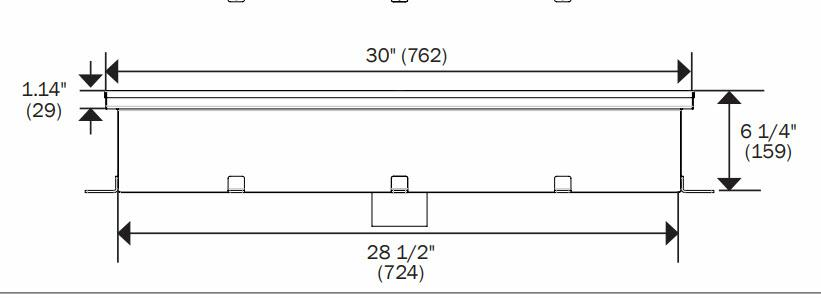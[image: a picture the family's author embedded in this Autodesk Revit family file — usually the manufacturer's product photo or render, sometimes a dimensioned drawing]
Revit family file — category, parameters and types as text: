
# Revit family: P5000
name_source: partatom
category: Plumbing Fixtures
revit_build: Autodesk Revit 2018 (Build: 20170223_1515(x64)
units: mm (PartAtom-declared; Revit-internal decimal feet)

## family parameters
Cut with Voids When Loaded = No
Host = Face
Part Type = Normal
Room Calculation Point = No
Round Connector Dimension = Use Radius
Shared = No

## types (36) — shared parameters
Banding = Yes
Banding Thickness = 0' - 0 1/8"
Cross Bar Offset = 0' - 2"
Cross Bar Spacing = 0' - 2"
Cross Bar Thickness = 0' - 0 1/8"
Default Elevation = 0' - 0"
Description = STAINLESS STEEL KETTLE DRAIN
Grate and Frame
Floor Drain Material = Paint - Sherwin Williams Paint - #952C2A - Bellwood Red
Height of Grating = 0' - 1 3/8"
Manufacturer = MIFAB
Material = Metal - Steel - ASTM A36
Support Bar Offset = 0' - 0 1/8"
Support Bar Spacing = 0' - 1"
Support Bar Thickness = 0' - 0 1/8"
URL = WWW.MIFAB.COM
zero-valued in all types: CWFU, WFU

## per-type parameters (varying)
| type | Length | Length2 | Model | Number of Cross Bars | Number of Support Bars | Pipe Radius | Support Bar Length | Width | Width2 |
| P5001 - 12" x 24" | 2' - 0" | 1' - 11 3/4" | P5001 | 5 | 24 | 0' - 2" | 0' - 11 1/2" | 1' - 0" | 0' - 11 3/4" |
| P5002 - 12" x 30" | 2' - 6" | 2' - 5 3/4" | P5002 | 5 | 30 | 0' - 2" | 0' - 11 1/2" | 1' - 0" | 0' - 11 3/4" |
| P5003 - 12" x 36" | 3' - 0" | 2' - 11 3/4" | P5003 | 5 | 36 | 0' - 2" | 0' - 11 1/2" | 1' - 0" | 0' - 11 3/4" |
| P5004 - 12" x 48" | 4' - 0" | 3' - 11 3/4" | P5004 | 5 | 48 | 0' - 2" | 0' - 11 1/2" | 1' - 0" | 0' - 11 3/4" |
| P5004 -60 - 12" x 60" | 5' - 0" | 4' - 11 3/4" | P5004-60 | 5 | 60 | 0' - 2" | 0' - 11 1/2" | 1' - 0" | 0' - 11 3/4" |
| P5004-72 - 12" x 72" | 6' - 0" | 5' - 11 3/4" | P5004-72 | 5 | 72 | 0' - 2" | 0' - 11 1/2" | 1' - 0" | 0' - 11 3/4" |
| P5004-84- 12" x 84" | 7' - 0" | 6' - 11 3/4" | P5004-84 | 5 | 84 | 0' - 2" | 0' - 11 1/2" | 1' - 0" | 0' - 11 3/4" |
| P5004-96 - 12" x 96" | 8' - 0" | 7' - 11 3/4" | P5004-96 | 5 | 96 | 0' - 2" | 0' - 11 1/2" | 1' - 0" | 0' - 11 3/4" |
| P5004-108 - 12" x 108" | 9' - 0" | 8' - 11 3/4" | P5004-108 | 5 | 108 | 0' - 2" | 0' - 11 1/2" | 1' - 0" | 0' - 11 3/4" |
| P5004-120 - 12" x 120" | 10' - 0" | 9' - 11 3/4" | P5004-120 | 5 | 120 | 0' - 2" | 0' - 11 1/2" | 1' - 0" | 0' - 11 3/4" |
| P5005 - 18" x 18" | 1' - 6" | 1' - 5 3/4" | P5005 | 8 | 18 | 0' - 3" | 1' - 5 1/2" | 1' - 6" | 1' - 5 3/4" |
| P5006 - 18" x 24" | 2' - 0" | 1' - 11 3/4" | P5006 | 8 | 24 | 0' - 3" | 1' - 5 1/2" | 1' - 6" | 1' - 5 3/4" |
| P5007 - 18" x 30" | 2' - 6" | 2' - 5 3/4" | P5007 | 8 | 30 | 0' - 3" | 1' - 5 1/2" | 1' - 6" | 1' - 5 3/4" |
| P5008 - 18" x 36" | 3' - 0" | 2' - 11 3/4" | P5008 | 8 | 36 | 0' - 3" | 1' - 5 1/2" | 1' - 6" | 1' - 5 3/4" |
| P5009 - 18" x 48" | 4' - 0" | 3' - 11 3/4" | P5009 | 8 | 48 | 0' - 3" | 1' - 5 1/2" | 1' - 6" | 1' - 5 3/4" |
| P5009-60 - 18" x 60" | 5' - 0" | 4' - 11 3/4" | P5009-60 | 8 | 60 | 0' - 3" | 1' - 5 1/2" | 1' - 6" | 1' - 5 3/4" |
| P5009-72 - 18" x 72" | 6' - 0" | 5' - 11 3/4" | P5009-72 | 8 | 72 | 0' - 3" | 1' - 5 1/2" | 1' - 6" | 1' - 5 3/4" |
| P5009-84 - 18" x 84" | 7' - 0" | 6' - 11 3/4" | P5009-84 | 8 | 84 | 0' - 3" | 1' - 5 1/2" | 1' - 6" | 1' - 5 3/4" |
| P5009-96 - 18" x 96" | 8' - 0" | 7' - 11 3/4" | P5009-96 | 8 | 96 | 0' - 3" | 1' - 5 1/2" | 1' - 6" | 1' - 5 3/4" |
| P5009-108 - 18" x 108" | 9' - 0" | 8' - 11 3/4" | P5009-108 | 8 | 108 | 0' - 3" | 1' - 5 1/2" | 1' - 6" | 1' - 5 3/4" |
| P5009-120 - 18" x 120" | 10' - 0" | 9' - 11 3/4" | P5009-120 | 8 | 120 | 0' - 3" | 1' - 5 1/2" | 1' - 6" | 1' - 5 3/4" |
| P5010 - 24" x 24" | 2' - 0" | 1' - 11 3/4" | P5010 | 11 | 24 | 0' - 4" | 1' - 11 1/2" | 2' - 0" | 1' - 11 3/4" |
| P5011 - 24" x 30" | 2' - 6" | 2' - 5 3/4" | P5011 | 11 | 30 | 0' - 4" | 1' - 11 1/2" | 2' - 0" | 1' - 11 3/4" |
| P5012 - 24" x 36" | 3' - 0" | 2' - 11 3/4" | P5012 | 11 | 36 | 0' - 4" | 1' - 11 1/2" | 2' - 0" | 1' - 11 3/4" |
| P5013 - 24" x 48" | 3' - 0" | 2' - 11 3/4" | P5013 | 11 | 36 | 0' - 4" | 1' - 11 1/2" | 2' - 0" | 1' - 11 3/4" |
| P5013-60 - 24" x 60" | 5' - 0" | 4' - 11 3/4" | P5013-60 | 11 | 60 | 0' - 4" | 1' - 11 1/2" | 2' - 0" | 1' - 11 3/4" |
| P5013-72 - 24" x 72" | 6' - 0" | 5' - 11 3/4" | P5013-72 | 11 | 72 | 0' - 4" | 1' - 11 1/2" | 2' - 0" | 1' - 11 3/4" |
| P5013-84 - 24" x 84" | 7' - 0" | 6' - 11 3/4" | P5013-84 | 11 | 84 | 0' - 4" | 1' - 11 1/2" | 2' - 0" | 1' - 11 3/4" |
| P5013-96 - 24" x96" | 8' - 0" | 7' - 11 3/4" | P5013-96 | 11 | 96 | 0' - 4" | 1' - 11 1/2" | 2' - 0" | 1' - 11 3/4" |
| P5013-108 - 24" x 108" | 9' - 0" | 8' - 11 3/4" | P5013-108 | 11 | 108 | 0' - 4" | 1' - 11 1/2" | 2' - 0" | 1' - 11 3/4" |
| P5013-120 - 24" x 120" | 10' - 0" | 9' - 11 3/4" | P5013-120 | 11 | 120 | 0' - 4" | 1' - 11 1/2" | 2' - 0" | 1' - 11 3/4" |
| P5014 - 30" x 30" | 2' - 6" | 2' - 5 3/4" | P5014 | 14 | 30 | 0' - 4" | 2' - 5 1/2" | 2' - 6" | 2' - 5 3/4" |
| P5015 - 30" x 36" | 3' - 0" | 2' - 11 3/4" | P5015 | 14 | 36 | 0' - 4" | 2' - 5 1/2" | 2' - 6" | 2' - 5 3/4" |
| P5016 - 30" x 48" | 4' - 0" | 3' - 11 3/4" | P5016 | 14 | 48 | 0' - 4" | 2' - 5 1/2" | 2' - 6" | 2' - 5 3/4" |
| P5017 - 36" x 36" | 3' - 0" | 2' - 11 3/4" | P5017 | 17 | 36 | 0' - 4" | 2' - 11 1/2" | 3' - 0" | 2' - 11 3/4" |
| P5018 - 36" x 38" | 4' - 0" | 3' - 11 3/4" | P5017 | 17 | 48 | 0' - 4" | 2' - 11 1/2" | 3' - 0" | 2' - 11 3/4" |

## geometry (parser evidence)
native form markers: Blend x1, Sweep x18
no freeform markers — native parametric forms only
